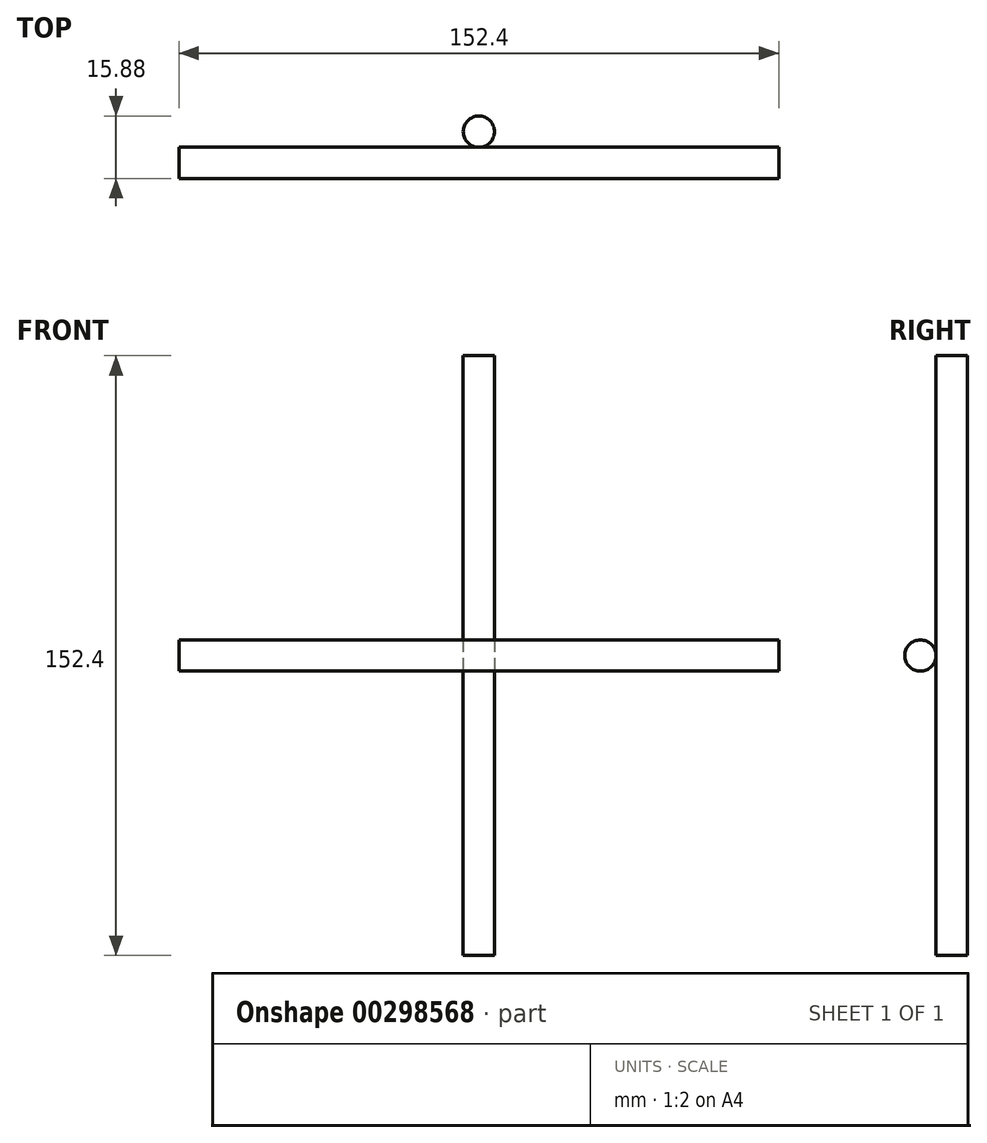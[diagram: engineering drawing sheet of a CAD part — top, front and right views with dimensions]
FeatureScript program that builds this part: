
annotation { "Feature Type Name" : "Feature", "Feature Type Description" : "" }
export const myFeature = defineFeature(function(context is Context, id is Id, definition is map)
    precondition{}
    {
        {
            var Q0;
            Q0=qCreatedBy(makeId("Top.planeOp"),FACE);
            var sketch = newSketch(context, id + "F0", { "sketchPlane" : qUnion([Q0])});
            skCircle(sketch, "E0", {"center": v(0, 0) * mm, "radius": 3.97 * mm});
            skSolve(sketch);
        }
        {
            var Q0;
            Q0=makeQuery(id+"F0.imprint","IMPRINT",FACE,{"disambiguationData":[TD([[makeQuery(id+"F0.imprint","IMPRINT",EDGE,{"derivedFrom":sQuery(id+"F0.wireOp",EDGE,"E0")}),1.0]])]});
            var Q1;
            Q1=sQuery(id+"F0.wireOp",EDGE,"E0");
            extrude(context, id + "F1", {"entities" : qUnion([Q0]), "surfaceEntities" : qUnion([Q1]), "endBound" : BoundingType.SYMMETRIC, "depth" : 152.4 * mm});
        }
        {
            var Q0;
            Q0=qCreatedBy(makeId("Right.planeOp"),FACE);
            var sketch = newSketch(context, id + "F2", { "sketchPlane" : qUnion([Q0])});
            skLineSegment(sketch, "E1", {"start": v(0, 0) * mm, "end": v(-7.94, 0) * mm, "construction": true});
            skCircle(sketch, "E2", {"center": v(-7.94, 0) * mm, "radius": 3.97 * mm});
            skSolve(sketch);
        }
        {
            var Q0;
            Q0 = qSketchRegion(id + "F2", true);
            extrude(context, id + "F3", {"entities" : qUnion([Q0]), "endBound" : BoundingType.SYMMETRIC, "depth" : 152.4 * mm});
        }
    });
